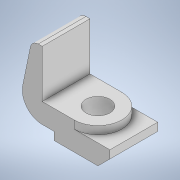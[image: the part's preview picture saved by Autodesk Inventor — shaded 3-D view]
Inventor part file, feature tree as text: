
AUTODESK INVENTOR PART (.ipt)
format: ipt  version: 2020 (Build 240168000, 168)  size: 137,728 bytes
history: native  units: in
note: dims shown in document units (in); Inventor stores cm internally (conversion verified against a paired STEP export)
features: sketch x3, extrude x2, hole x1
ambient origin geometry x8: Origin, YZ Plane, XZ Plane, XY Plane, X Axis, Y Axis, Z Axis, Center Point
bodies: Solid1 (feature_tree)
feature tree (6):
  extrude  "Extrusion1"  Depth=2.75in
  extrude  "Extrusion2"  Depth=3.0in
  hole  "Hole1"  [1 undecoded]
  sketch  "Sketch1"  dims[d0=0.25in d1=2.75in]
  sketch  "Sketch2"  dims[d2=0.5in d3=3.0in]
  sketch  "Sketch3"  dims[d4=2.5in d5=0.75in d7=1.25in d8=4.25in d9=1.0in d10=0.5in d11=2.0in d12=1.75in d13=3.0in d14=0.0in d15=3.0in d16=0.0in d17=1.5in d18=0.75in d19=0.375in d20=0.25in d21=0.5635in d22=1.0in d23=0.8108in]
note: 1 required parameter value undecoded (feature->parameter linkage not recoverable at this tier; creation-order binding heuristic only, values carry confidence <= 0.55)
